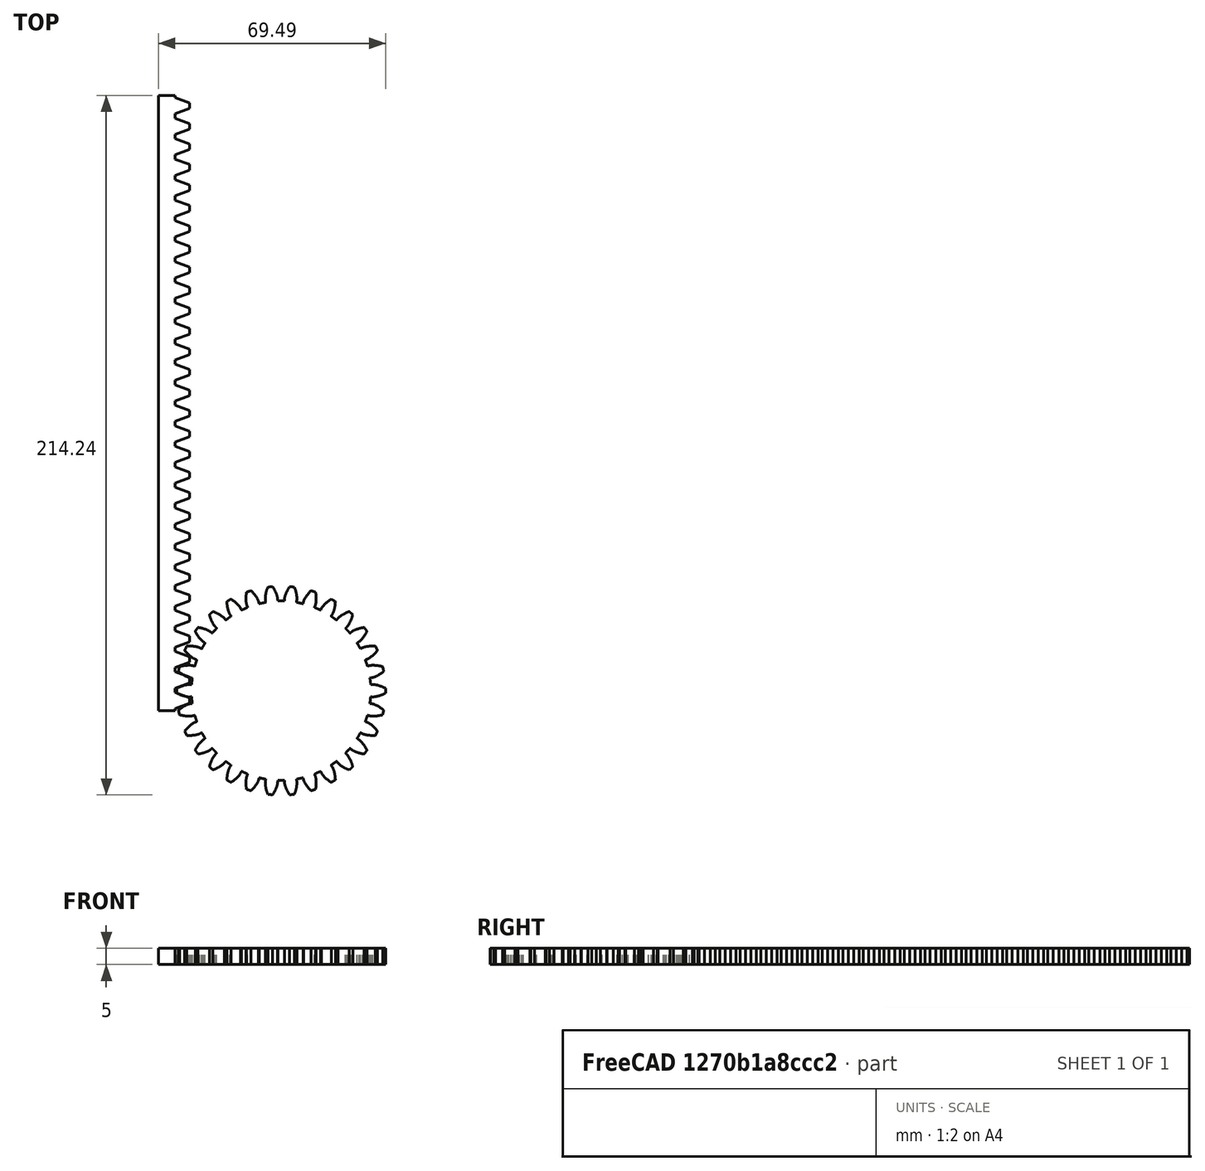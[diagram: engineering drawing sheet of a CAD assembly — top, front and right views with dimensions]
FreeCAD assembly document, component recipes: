
FREECAD ASSEMBLY — COMPONENT RECIPES ("part1")

This assembly document has 2 components, labeled P0..P1 below (a component is one placed body or linked part). 0 of them carry a construction recipe — the FreeCAD feature program that regenerates the part from scratch, quoted from this document or its linked companion documents; the rest are supplied as boundary geometry only. No exploded tour is included for this assembly.
COMPONENT P0 — geometry summary ("c-gear"; no construction recipe available for this part):
  bounding box: 64.0 x 63.8 x 5.0 mm
  tessellated surface: 716 triangles
  volume: 13941 mm^3 (68% of its bounding box)
  symmetry: 2-fold rotationally symmetric about the x axis; 2-fold rotationally symmetric about the y axis; 6-fold rotationally symmetric about the z axis; mirror-symmetric across its x mid-plane, z mid-plane
COMPONENT P1 — geometry summary ("sh-gear"; no construction recipe available for this part):
  bounding box: 188.5 x 9.5 x 5.0 mm
  tessellated surface: 492 triangles
  volume: 6956 mm^3 (78% of its bounding box)
  symmetry: 2-fold rotationally symmetric about the x axis; mirror-symmetric across its y mid-plane, z mid-plane
PROVENANCE & LICENSES
A FreeCAD (.FCStd) document from a public repository crawl; recipes are the document's own serialized feature recipes (and, for linked parts, companion documents' recipes).
License: as declared in the source repository (recorded in the dataset sidecar).
